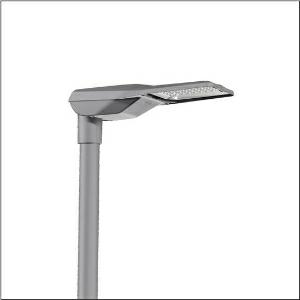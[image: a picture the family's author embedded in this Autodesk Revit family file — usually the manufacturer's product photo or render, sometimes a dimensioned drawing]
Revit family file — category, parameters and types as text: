
# Revit family: streetlight_sl_21_iq_mini___p0_5a_5xe2v31d08gb_51ef
name_source: partatom
category: Lighting Fixtures
units: mm (PartAtom-declared; Revit-internal decimal feet)

## family parameters
Cut with Voids When Loaded = No
Host = Face
Light Source = No
Part Type = Normal
Room Calculation Point = No
Round Connector Dimension = Use Diameter
Shared = No

## types (1)
- --- (1 x LED, 5580 lm, 37.1 W, 3000K)
    Apparent Load = 37 VA
    CIE Flux Codes = 37 73 96 100 100
    Color Rendering = 70
    Color Temperature = 3000K
    Default Elevation = 1800 mm
    Description = Streetlight SL 21 iQ mini, mast luminaire, primary light control with lens, of PMMA, primary optical cover: cover, of toughened safety glass, transparent, light distribution: P0.5a, light emission: direct distribution, primary light characteristic: asymmetric, installation type: post-top, side-entry, LED, High Power LED, rated luminous flux: 5.580lm, luminous efficacy: 150lm/W, light colour: 730, colour temperature: 3000K, control gear: iQ-Comfort, control: pre-setting: linear dimming characteristic, Auto-Match, Temp-Guard, Lumen-Switch, Night-Set, Smart-Wire, Light-Fading, Desk-Remote (wireless, voltage-free reading and setting of iQ features in the workshop via application-optimized NFC function/RFID function), optimised constant luminous flux control (CLO 2.0), mains connection: 220..240V, AC, 50/60Hz, start of lifetime: 37W, end of service life: 39W, reduction: 18W, luminaire housing, of diecast aluminium, powder-coated, Siteco® metallic grey (DB 702S), corrosivity category C5 mid according to DIN EN ISO 12944, please order mast flange separately, inclination adjustable: 0°, 5°, 10°, 15°, sealing non-destructively replaceable, multi-level sealing system, length: 628mm, width: 235mm, height: 110mm, mast flange for spigot size: 42mm (side-entry): 5XC10008XM4, 60/48mm (side-entry/post-top): 5XC10108XM2, 76/60mm (side-entry/post-top): 5XC10108XM1, mounting height: 4..8m, protection rating (complete): IP66, insulation class (complete): insulation class II (safety insulation), certification: CE, ENEC, ENEC+, VDE, impact resistance: IK10, permissible operating ambient temperature for outdoor applications: -40..+50°C, standard-compliant lighting for roads and squares, packaging unit: 1 piece

Light Distribution: P0.5a
    Height = 110 mm
    Lamp = 1 x LED
    Lamp Light Flux = 5580 lm
    Lamp Power = 37.1 W
    Lamp count = 1
    Length = 625 mm
    Luminous efficacy = 150 lm/W
    Manufacturer = Siteco
    ModVariant = No
    Model = 5XE2V31D08GB
    Number of Poles = 1
    OnlyDefault = Yes
    Power Factor = 1
    Product Name = Streetlight SL 21 iQ mini | P0.5a
    Product group = mast luminaire | pylon top
    ProductGroupID = 6100
    Protection Class = Protection class II
    Protection Degree = IP 66
    RLX_Detail_Level = 1
    RLX_Emergency_Light_Flux = 0 lm
    RLX_Emergency_Type = 0
    RLX_Emergency_Type_DB = No
    RlxData = <blob elided: 25881 chars, md5=6d6e4f00>
    Socket = socket
    Standby Power = 0 W
    System Light Flux = 5580 lm
    System Power = 37 W
    Type Comments = factory setting: luminous flux: 100 % | dim-lin: 254 | 385 mA
    Type Image = l_1003519.jpg
    URL = http://relux.com
    VarID = @adj_070028
    Voltage = 0 V
    Weight = 0.00 kg
    Width = 234 mm

## geometry (parser evidence)
native form markers: Blend x4, Sweep x10
no freeform markers — native parametric forms only
